# Revit family: QF_BPRO_KTTW 4_575109
name_source: partatom
category: Sonderausstattung
revit_build: Autodesk Revit 2018 (Build: 20181015_0930(x64)
units: mm (PartAtom-declared; Revit-internal decimal feet)

## family parameters
Arbeitsebenenbasiert = Nein
Beim Laden mit Abzugskörper schneiden = Nein
Bemaßung runder Anschluss = Durchmesser verwenden
Gemeinsam genutzt = Nein
Immer vertikal = Ja
Raumberechnungspunkt = Nein
Teiletyp = Normal

## types (1)
- KTTW 4
    Artikel Nummer = 575109
    Beschreibung = KTTW 4
Systemteilewagen mit 4 Ablagen,
mit Durchschubsicherung,
komplett aus Edelstahl, dient zur Lagerung
von Systemteilen (Kompakttablett
Unter- und Oberteile)
Maß Auflagefläche: 1150 x 537 mm
Lichtes Maß zwischen
den Auflageflächen: 404 mm
Kapazität: ca. 60 – 80 Unter- und
Oberteile
    Beschreibung durch Hersteller analog Leistungsverzeichnislangtext = Abmessungen

Länge:			1276 mm
Breite:		663 mm  
Höhe:		1801 mm


Ausführung

Der Systemteilewagen besteht komplett aus CNS 18/10 und dient zur Lagerung von Systemteilen (Kompakttablett Unter- und Oberteile). 
Das Rahmengestell besteht aus stabilen Vierkantrohr 25x25 mm. Dazwischen sind 4 Tragrahmen eingeschweißt, die zur Aufnahme lose eingelegter Roste dienen. Die Roste sind speziell für die Lagerung der o.g. Systemteile ausgerichtet. Stirnseitig sind auf jeder Seite jeweils 2 Vierkantrohre als zusätzliche Verstärkung und Kippsicherung der eingestellten Systemteile vertikal eingeschweißt. Darüber hinaus ist der Systemteilewagen mit einer längsseitigen Durchschubsicherung aus einem eingeschweißten Vierkantrohr je Auflagefläche ausgestattet.

Der Systemteilewagen ist fahrbar mittels rostfreien Kunststoffrollen gemäß DIN 18867-8 (2 Block- und 2 Lenkrollen mit Feststeller, Rollendurchmesser 125 mm). An allen vier Ecken befinden sich runde Wandabweiser.


Technische Daten

Werkstoff:		CNS 18/10
Gewicht:		39 kg
Auflageflächen: 	4 Stück
Maß Auflagefläche:	1150 x 537 mm  
Lichtes Maß zwischen 
den Auflageflächen:	404 mm
Kapazität:	ca. 60 – 80 Unter- und Oberteile	
			
				
Besonderheit

•	mit längsseitiger Durchschubsicherung je Auflagefläche


Fabrikat

Hersteller:		 	B.PRO
Modell:                                	KTTW 4
Best.Nr.	575 109
    CE Kennzeichnung = Ja
    Gerätegewicht Netto = 27.00 kg
    Großküchengerätezuordnung = Ja
    Hersteller = B.PRO GmbH
    Höhe = 1801 mm
    Internetadresse Gerätehersteller = https://www.bpro-solutions.com
    Kosten = 1279 $
    Länge Gerätebreite = 663 mm
    Material = QF_Metal-Stainless-Steel_general
    Material Rollen = QF_Plastic-Dark_Grey-Matt
    Material Stoßschutz = QF_Plastic-Dark_Grey-Matt
    Modell = KTTW 4
    Tiefe = 1276 mm
    Typenkommentare = Systemteilewagen
    URL = https://www.bpro-solutions.com
    Zubehör = Ja
